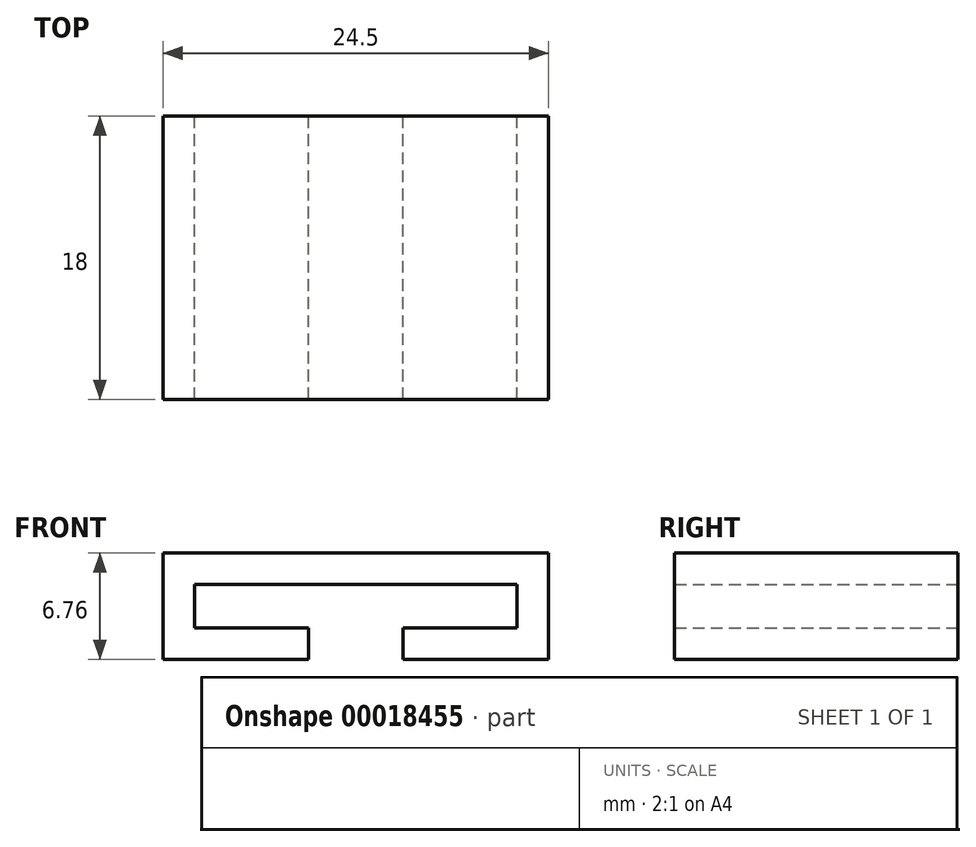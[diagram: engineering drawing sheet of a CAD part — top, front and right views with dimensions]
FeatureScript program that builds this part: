
annotation { "Feature Type Name" : "Feature", "Feature Type Description" : "" }
export const myFeature = defineFeature(function(context is Context, id is Id, definition is map)
    precondition{}
    {
        {
            var Q0;
            Q0=qCreatedBy(makeId("Front.planeOp"),FACE);
            var sketch = newSketch(context, id + "F0", { "sketchPlane" : qUnion([Q0])});
            skLineSegment(sketch, "E0.rect.bottom", {"start": v(10.25, -1.37) * mm, "end": v(-10.25, -1.37) * mm});
            skLineSegment(sketch, "E0.rect.top", {"start": v(10.25, 1.38) * mm, "end": v(-10.25, 1.38) * mm});
            skLineSegment(sketch, "E0.rect.left", {"start": v(10.25, -1.37) * mm, "end": v(10.25, 1.38) * mm});
            skLineSegment(sketch, "E0.rect.right", {"start": v(-10.25, -1.37) * mm, "end": v(-10.25, 1.37) * mm});
            skPoint(sketch, "E0.rect.middle", {"position": v(0, 0) * mm});
            skLineSegment(sketch, "E1.0", {"start": v(12.25, 3.38) * mm, "end": v(-12.25, 3.38) * mm});
            skLineSegment(sketch, "E1.1", {"start": v(12.25, -3.37) * mm, "end": v(12.25, 3.38) * mm});
            skLineSegment(sketch, "E1.2", {"start": v(12.25, -3.37) * mm, "end": v(-12.25, -3.37) * mm});
            skLineSegment(sketch, "E1.3", {"start": v(-12.25, -3.37) * mm, "end": v(-12.25, 3.37) * mm});
            skPoint(sketch, "E2", {"position": v(0, -1.37) * mm});
            skLineSegment(sketch, "E3.bottom", {"start": v(-3, -3.37) * mm, "end": v(3, -3.37) * mm});
            skLineSegment(sketch, "E3.top", {"start": v(-3, -1.37) * mm, "end": v(3, -1.37) * mm});
            skLineSegment(sketch, "E3.left", {"start": v(-3, -3.37) * mm, "end": v(-3, -1.37) * mm});
            skLineSegment(sketch, "E3.right", {"start": v(3, -3.37) * mm, "end": v(3, -1.37) * mm});
            skSolve(sketch);
        }
        {
            var Q0;
            Q0=makeQuery(id+"F0.imprint","IMPRINT",FACE,{"disambiguationData":[TD([[makeQuery(id+"F0.imprint","IMPRINT",EDGE,{"derivedFrom":sQuery(id+"F0.wireOp",EDGE,"E0.rect.top")}),-1.0]])]});
            extrude(context, id + "F1", {"entities" : qUnion([Q0]), "depth" : 18 * mm});
        }
    });
